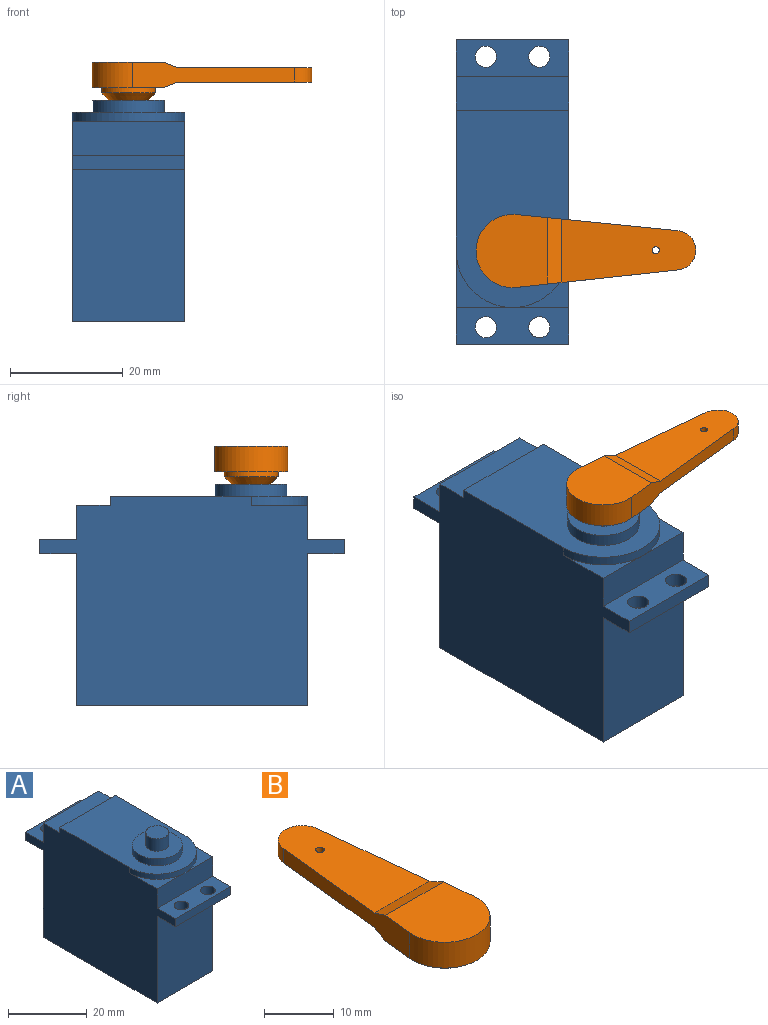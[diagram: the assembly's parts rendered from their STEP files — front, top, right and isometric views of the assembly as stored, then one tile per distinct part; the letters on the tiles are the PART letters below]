
ASSEMBLY  parts=2 mates=1
PART A: 27 faces, bbox 20x54x43.2 mm
  f0: plane 20x6mm, normal (0,0,1), area 120mm2, adj f4,f6,f14,f17
  f1: plane 10x10mm, normal (0,0,1), area 21.5mm2, adj f6,f13,f16
  f2: plane 20x6.5mm, normal (0,0,1), area 107.9mm2, adj f4,f6,f10,f14,f25,f26
  f3: plane 27x20mm, normal (0,-1,0), area 540mm2, adj f4,f6,f7,f12
  f4: plane 54x37.21mm, normal (1,0,0), area 1531.7mm2, adj f0,f2,f3,f5,f7,f8,f9,f10
  f5: plane 27x20mm, normal (0,1,0), area 540mm2, adj f4,f6,f7,f8
  f6: plane 54x37.21mm, normal (-1,0,0), area 1531.7mm2, adj f0,f1,f2,f3,f5,f7,f8,f9
  f7: plane 41x20mm, normal (0,0,-1), area 820mm2, adj f3,f4,f5,f6
  f8: plane 20x6.5mm, normal (0,0,-1), area 107.9mm2, adj f4,f5,f6,f10,f25,f26
  f9: plane 20x2.5mm, normal (0,-1,0), area 50mm2, adj f4,f6,f11,f12
  f10: plane 20x2.5mm, normal (0,1,0), area 50mm2, adj f2,f4,f6,f8
  f11: plane 20x6.5mm, normal (0,0,1), area 107.9mm2, adj f4,f6,f9,f13,f23,f24
  f12: plane 20x6.5mm, normal (0,0,-1), area 107.9mm2, adj f3,f4,f6,f9,f23,f24
  f13: plane 20x6.06mm, normal (0,-1,0), area 121.2mm2, adj f1,f4,f6,f11,f15
  f14: plane 20x6.06mm, normal (0,1,0), area 121.2mm2, adj f0,f2,f4,f6
  f15: plane 10x10mm, normal (0,0,1), area 21.5mm2, adj f4,f13,f16
  f16: cylinder r=10mm len=20mm, axis (0,0,-1), area 51.9mm2, adj f1,f4,f6,f15,f18
  f17: plane 20x1.65mm, normal (0,1,0), area 33mm2, adj f0,f4,f6,f18
  f18: plane 35x20mm, normal (0,0,1), area 530.4mm2, adj f4,f6,f16,f17,f19
  f19: cylinder r=6.35mm len=12.7mm, axis (0,0,-1), area 86.1mm2, adj f18,f20
  f20: plane 12.7x12.7mm, normal (0,0,1), area 99.9mm2, adj f19,f21
  f21: cylinder r=2.92mm len=5.84mm, axis (0,0,-1), area 69.9mm2, adj f20,f22
  f22: plane 5.84x5.84mm, normal (0,0,1), area 26.8mm2, adj f21
  f23: cylinder r=1.88mm len=3.75mm, axis (0,0,1), area 29.5mm2, adj f11,f12
  f24: cylinder r=1.88mm len=3.75mm, axis (0,0,1), area 29.5mm2, adj f11,f12
  f25: cylinder r=1.88mm len=3.75mm, axis (0,0,1), area 29.5mm2, adj f2,f8
  f26: cylinder r=1.88mm len=3.75mm, axis (0,0,1), area 29.5mm2, adj f2,f8
PART B: 16 faces, bbox 13x39x6.7 mm
  f0: plane 11.78x2.54mm, normal (0,0.37,0.93), area 31.5mm2, adj f2,f5,f7,f8
  f1: plane 11.78x2.54mm, normal (0,0.37,-0.93), area 31.5mm2, adj f3,f5,f7,f9
  f2: plane 13x12.7mm, normal (0,0,1), area 143.4mm2, adj f0,f4,f5,f7
  f3: plane 13x12.7mm, normal (0,0,-1), area 72.1mm2, adj f1,f4,f5,f7,f10
  f4: cylinder r=6.5mm len=13mm, axis (0,0,-1), area 99mm2, adj f2,f3,f5,f7
  f5: plane 28.69x4.55mm, normal (0.99,0.1,0), area 87mm2, adj f0,f1,f2,f3,f4,f6,f8,f9
  f6: cylinder r=3.5mm len=6.96mm, axis (0,0,-1), area 26.1mm2, adj f5,f7,f8,f9
  f7: plane 28.69x4.55mm, normal (-0.99,0.1,0), area 87mm2, adj f0,f1,f2,f3,f4,f6,f8,f9
  f8: plane 23.76x11.25mm, normal (0,0,1), area 203.3mm2, adj f0,f5,f6,f7,f15
  f9: plane 23.76x11.25mm, normal (0,0,-1), area 203.3mm2, adj f1,f5,f6,f7,f15
  f10: cylinder r=4.76mm len=9.53mm, axis (0,0,1), area 27.4mm2, adj f3,f12
  f11: plane 6.99x6.99mm, normal (0,0,-1), area 11.5mm2, adj f12,f13
  f12: cone r=3.49mm half-angle=45deg, axis (0,0,1), area 46.6mm2, adj f10,f11
  f13: cylinder r=2.92mm len=5.84mm, axis (0,0,-1), area 93.2mm2, adj f11,f14
  f14: plane 5.84x5.84mm, normal (0,0,-1), area 26.8mm2, adj f13
  f15: cylinder r=0.64mm len=2.54mm, axis (0,0,1), area 10.1mm2, adj f8,f9
PLACE A at identity fixed
PLACE B rot(axis=(0,0,-1),89.7deg) t=(0,-10.5,43.83)mm
MATE revolute B.f13 <-> A.f16  axis (0,0,-1) through (0,-10.5,39.37)mm
